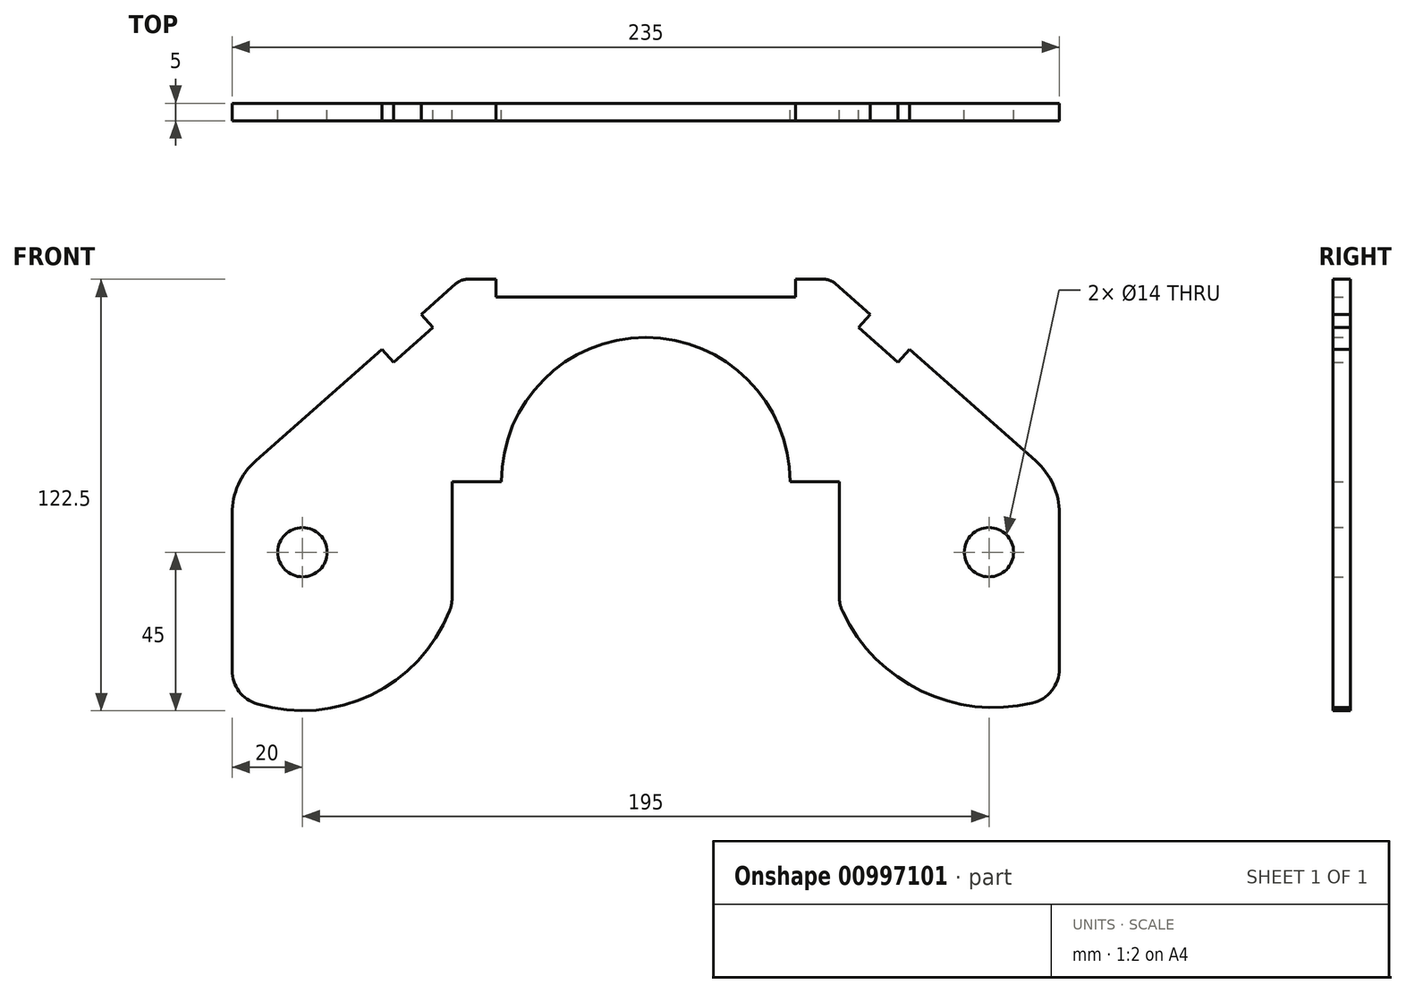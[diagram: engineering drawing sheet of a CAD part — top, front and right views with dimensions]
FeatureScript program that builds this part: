
annotation { "Feature Type Name" : "Feature", "Feature Type Description" : "" }
export const myFeature = defineFeature(function(context is Context, id is Id, definition is map)
    precondition{}
    {
        {
            var Q0;
            Q0=qCreatedBy(makeId("Front.planeOp"),FACE);
            var sketch = newSketch(context, id + "F0", { "sketchPlane" : qUnion([Q0])});
            skArc(sketch, "E0", {"start": v(41, 0) * mm, "mid": v(0, 41) * mm, "end": v(-41, 0) * mm});
            skCircle(sketch, "E1", {"center": v(-97.5, -20) * mm, "radius": 7 * mm});
            skCircle(sketch, "E2", {"center": v(97.5, -20) * mm, "radius": 7 * mm});
            skLineSegment(sketch, "E3", {"start": v(-55, 0) * mm, "end": v(-55, -33) * mm});
            skLineSegment(sketch, "E4", {"start": v(55, 0) * mm, "end": v(55, -32.68) * mm});
            skLineSegment(sketch, "E5", {"start": v(-55, 0) * mm, "end": v(-41, 0) * mm});
            skLineSegment(sketch, "E6", {"start": v(41, 0) * mm, "end": v(55, 0) * mm});
            skPoint(sketch, "E7.visualSharp", {"position": v(-55, -34.8) * mm});
            skLineSegment(sketch, "E8", {"start": v(-117.5, -53.54) * mm, "end": v(-117.5, -9.01) * mm});
            skLineSegment(sketch, "E9", {"start": v(-50.6, 57.5) * mm, "end": v(-42.5, 57.5) * mm});
            skLineSegment(sketch, "E10", {"start": v(117.5, -9.01) * mm, "end": v(117.5, -53.1) * mm});
            skLineSegment(sketch, "E11", {"start": v(-42.5, 57.5) * mm, "end": v(-42.5, 52.5) * mm});
            skLineSegment(sketch, "E12", {"start": v(-42.5, 52.5) * mm, "end": v(42.5, 52.5) * mm});
            skLineSegment(sketch, "E13", {"start": v(42.5, 52.5) * mm, "end": v(42.5, 57.5) * mm});
            skLineSegment(sketch, "E14.trimOffspring", {"start": v(42.5, 57.5) * mm, "end": v(50.6, 57.5) * mm});
            skArc(sketch, "E15.trimOffspring", {"start": v(-110.36, -63.12) * mm, "mid": v(-77.91, -60.51) * mm, "end": v(-55.71, -36.7) * mm});
            skPoint(sketch, "E16", {"position": v(0, 52.5) * mm});
            skPoint(sketch, "E17.visualSharp", {"position": v(117.5, 57.5) * mm});
            skPoint(sketch, "E18.visualSharp", {"position": v(117.5, -60.31) * mm});
            skPoint(sketch, "E19.visualSharp", {"position": v(55, -34.8) * mm});
            skPoint(sketch, "E20.visualSharp", {"position": v(-117.5, -60.31) * mm});
            skPoint(sketch, "E21.visualSharp", {"position": v(-117.5, 57.5) * mm});
            skArc(sketch, "E22", {"start": v(55.96, -36.96) * mm, "mid": v(78.3, -59.42) * mm, "end": v(109.8, -62.84) * mm});
            skArc(sketch, "E23.filletArc", {"start": v(-55.71, -36.7) * mm, "mid": v(-55.18, -34.88) * mm, "end": v(-55, -33) * mm});
            skArc(sketch, "E24.filletArc", {"start": v(-117.5, -53.54) * mm, "mid": v(-115.52, -59.52) * mm, "end": v(-110.36, -63.12) * mm});
            skArc(sketch, "E25.filletArc", {"start": v(55, -32.68) * mm, "mid": v(55.24, -34.87) * mm, "end": v(55.96, -36.96) * mm});
            skArc(sketch, "E26.filletArc", {"start": v(109.8, -62.84) * mm, "mid": v(115.34, -59.31) * mm, "end": v(117.5, -53.1) * mm});
            skLineSegment(sketch, "E27", {"start": v(53.92, 56.24) * mm, "end": v(63.73, 47.56) * mm});
            skLineSegment(sketch, "E28.MirrorCS", {"start": v(-53.92, 56.24) * mm, "end": v(-63.73, 47.56) * mm});
            skPoint(sketch, "E29.visualSharp", {"position": v(-52.5, 57.5) * mm});
            skArc(sketch, "E29.filletArc", {"start": v(-50.6, 57.5) * mm, "mid": v(-52.38, 57.18) * mm, "end": v(-53.92, 56.24) * mm});
            skPoint(sketch, "E30.visualSharp", {"position": v(52.5, 57.5) * mm});
            skArc(sketch, "E30.filletArc", {"start": v(53.92, 56.24) * mm, "mid": v(52.38, 57.18) * mm, "end": v(50.6, 57.5) * mm});
            skPoint(sketch, "E31.visualSharp", {"position": v(117.5, 0) * mm});
            skArc(sketch, "E31.filletArc", {"start": v(117.5, -9.01) * mm, "mid": v(115.73, -0.8) * mm, "end": v(110.75, 5.97) * mm});
            skPoint(sketch, "E32.newPointA", {"position": v(-117.5, 0) * mm});
            skArc(sketch, "E32.filletArc", {"start": v(-110.75, 5.97) * mm, "mid": v(-115.73, -0.8) * mm, "end": v(-117.5, -9.01) * mm});
            skLineSegment(sketch, "E33", {"start": v(-63.73, 47.56) * mm, "end": v(-60.42, 43.82) * mm});
            skLineSegment(sketch, "E34", {"start": v(-60.42, 43.82) * mm, "end": v(-71.66, 33.88) * mm});
            skLineSegment(sketch, "E35", {"start": v(-71.66, 33.88) * mm, "end": v(-74.97, 37.62) * mm});
            skLineSegment(sketch, "E36.trimOffspring", {"start": v(-74.97, 37.62) * mm, "end": v(-110.75, 5.97) * mm});
            skLineSegment(sketch, "E37.MirrorCS", {"start": v(63.73, 47.56) * mm, "end": v(60.42, 43.82) * mm});
            skLineSegment(sketch, "E38.MirrorCS", {"start": v(60.42, 43.82) * mm, "end": v(71.66, 33.88) * mm});
            skLineSegment(sketch, "E39.MirrorCS", {"start": v(71.66, 33.88) * mm, "end": v(74.97, 37.62) * mm});
            skLineSegment(sketch, "E40.trimOffspring", {"start": v(74.97, 37.62) * mm, "end": v(110.75, 5.97) * mm});
            skSolve(sketch);
        }
        {
            var Q0;
            Q0 = qSketchRegion(id + "F0", true);
            extrude(context, id + "F1", {"entities" : qUnion([Q0]), "depth" : 5 * mm, "offsetDistance" : 25 * mm});
        }
    });
